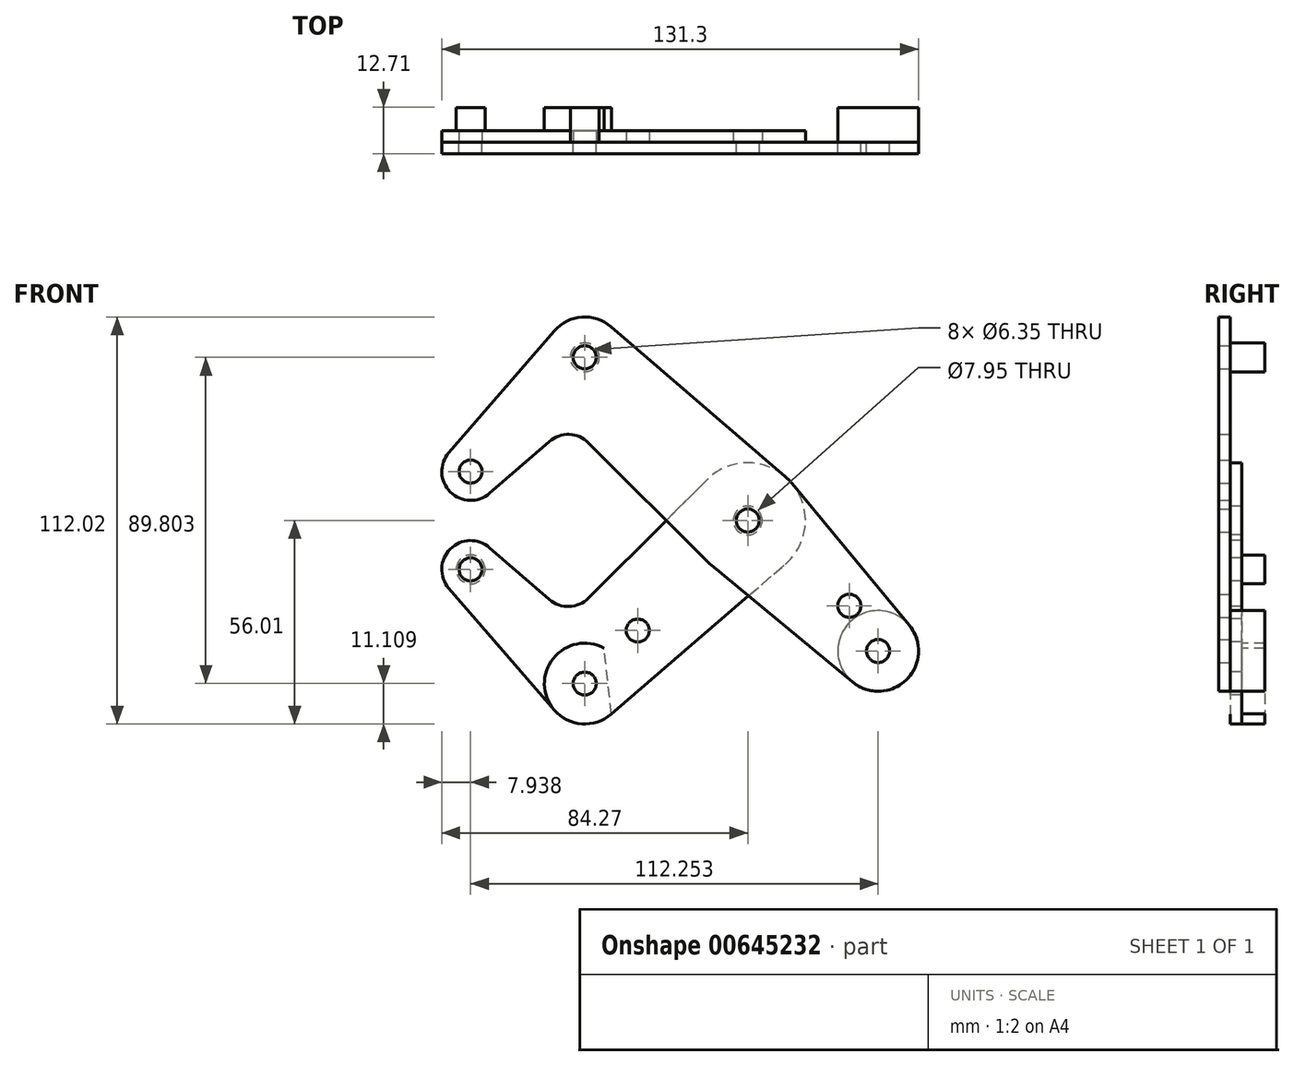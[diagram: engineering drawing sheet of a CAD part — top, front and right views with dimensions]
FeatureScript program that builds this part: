
annotation { "Feature Type Name" : "Feature", "Feature Type Description" : "" }
export const myFeature = defineFeature(function(context is Context, id is Id, definition is map)
    precondition{}
    {
        {
            var Q0;
            Q0=qCreatedBy(makeId("Front.planeOp"),FACE);
            var sketch = newSketch(context, id + "F0", { "sketchPlane" : qUnion([Q0])});
            skLineSegment(sketch, "E0", {"start": v(-76.33, 13.47) * mm, "end": v(-44.9, 44.9) * mm, "construction": true});
            skLineSegment(sketch, "E1", {"start": v(-44.9, 44.9) * mm, "end": v(35.92, -35.92) * mm, "construction": true});
            skCircle(sketch, "E2", {"center": v(-76.33, 13.47) * mm, "radius": 7.94 * mm});
            skCircle(sketch, "E3", {"center": v(-76.33, 13.47) * mm, "radius": 3.18 * mm});
            skCircle(sketch, "E4", {"center": v(-44.9, 44.9) * mm, "radius": 11.11 * mm});
            skCircle(sketch, "E5", {"center": v(-44.9, 44.9) * mm, "radius": 3.18 * mm});
            skCircle(sketch, "E6", {"center": v(0, 0) * mm, "radius": 15.88 * mm});
            skCircle(sketch, "E7", {"center": v(0, 0) * mm, "radius": 3.98 * mm});
            skCircle(sketch, "E8", {"center": v(0, 0) * mm, "radius": 3.18 * mm});
            skCircle(sketch, "E9", {"center": v(35.92, -35.92) * mm, "radius": 11.11 * mm});
            skCircle(sketch, "E10", {"center": v(35.92, -35.92) * mm, "radius": 3.18 * mm});
            skCircle(sketch, "E11", {"center": v(27.97, -23.48) * mm, "radius": 3.18 * mm});
            skLineSegment(sketch, "E12", {"start": v(0, 0) * mm, "end": v(-44.9, -44.9) * mm, "construction": true});
            skLineSegment(sketch, "E13", {"start": v(-44.9, -44.9) * mm, "end": v(-76.33, -13.47) * mm, "construction": true});
            skCircle(sketch, "E14", {"center": v(-76.33, -13.47) * mm, "radius": 7.94 * mm});
            skCircle(sketch, "E15", {"center": v(-76.33, -13.47) * mm, "radius": 3.18 * mm});
            skCircle(sketch, "E16", {"center": v(-44.9, -44.9) * mm, "radius": 11.11 * mm});
            skCircle(sketch, "E17", {"center": v(-44.9, -44.9) * mm, "radius": 3.18 * mm});
            skCircle(sketch, "E18", {"center": v(-30.3, -30.3) * mm, "radius": 3.18 * mm});
            skLineSegment(sketch, "E19", {"start": v(-76.33, 13.47) * mm, "end": v(-76.33, -13.47) * mm, "construction": true});
            skLineSegment(sketch, "E20", {"start": v(-82.33, 18.67) * mm, "end": v(-53.3, 52.18) * mm});
            skLineSegment(sketch, "E21", {"start": v(-71.13, 7.47) * mm, "end": v(-54.65, 21.76) * mm});
            skLineSegment(sketch, "E22", {"start": v(-37.66, 53.33) * mm, "end": v(10.35, 12.04) * mm});
            skLineSegment(sketch, "E23", {"start": v(44.48, -28.83) * mm, "end": v(12.23, 10.12) * mm});
            skLineSegment(sketch, "E24", {"start": v(-43.82, 21.37) * mm, "end": v(-11.23, -11.23) * mm});
            skLineSegment(sketch, "E25", {"start": v(28.83, -44.48) * mm, "end": v(-10.12, -12.23) * mm});
            skPoint(sketch, "E26.newPointA", {"position": v(-37.66, 36.48) * mm});
            skArc(sketch, "E26.filletArc", {"start": v(-43.82, 21.37) * mm, "mid": v(-49.16, 23.7) * mm, "end": v(-54.65, 21.76) * mm});
            skLineSegment(sketch, "E27", {"start": v(-82.33, -18.67) * mm, "end": v(-53.3, -52.18) * mm});
            skLineSegment(sketch, "E28", {"start": v(-37.66, -53.33) * mm, "end": v(11.26, -11.26) * mm});
            skLineSegment(sketch, "E29", {"start": v(-71.13, -7.47) * mm, "end": v(-54.65, -21.76) * mm});
            skLineSegment(sketch, "E30", {"start": v(-43.82, -21.37) * mm, "end": v(-11.23, 11.23) * mm});
            skArc(sketch, "E31.filletArc", {"start": v(-54.65, -21.76) * mm, "mid": v(-49.16, -23.7) * mm, "end": v(-43.82, -21.37) * mm});
            skSolve(sketch);
        }
        {
            var Q0;
            Q0=makeQuery(id+"F0.imprint","IMPRINT",FACE,{"disambiguationData":[TD([[makeQuery(id+"F0.imprint","IMPRINT",EDGE,{"derivedFrom":sQuery(id+"F0.wireOp",EDGE,"E3")}),-1.0]])]});
            var Q1;
            Q1=makeQuery(id+"F0.imprint","IMPRINT",FACE,{"disambiguationData":[TD([[makeQuery(id+"F0.imprint","IMPRINT",EDGE,{"derivedFrom":sQuery(id+"F0.wireOp",EDGE,"E5")}),-1.0]])]});
            var Q2;
            Q2=makeQuery(id+"F0.imprint","IMPRINT",FACE,{"disambiguationData":[TD([[makeQuery(id+"F0.imprint","IMPRINT",EDGE,{"derivedFrom":sQuery(id+"F0.wireOp",EDGE,"E10")}),-1.0]])]});
            var Q3;
            {var subQ0=sQuery(id+"F0.wireOp",EDGE,"E24");var subQ1=sQuery(id+"F0.wireOp",EDGE,"E6");var subQ2=makeQuery(id+"F0.imprint","INTERSECT",VERTEX,{"derivedFrom":[subQ1,subQ0]});Q3=makeQuery(id+"F0.imprint","IMPRINT",FACE,{"disambiguationData":[TD([[makeQuery(id+"F0.imprint","IMPRINT",EDGE,{"disambiguationData":[TD([[subQ2,1.0]])],"derivedFrom":subQ1}),-1.0]])]});}
            var Q4;
            {var subQ0=sQuery(id+"F0.wireOp",EDGE,"E25");var subQ1=sQuery(id+"F0.wireOp",EDGE,"E6");var subQ2=makeQuery(id+"F0.imprint","INTERSECT",VERTEX,{"derivedFrom":[subQ1,subQ0]});Q4=makeQuery(id+"F0.imprint","IMPRINT",FACE,{"disambiguationData":[TD([[makeQuery(id+"F0.imprint","IMPRINT",EDGE,{"disambiguationData":[TD([[subQ2,-1.0]])],"derivedFrom":subQ1}),-1.0]])]});}
            var Q5;
            Q5=makeQuery(id+"F0.imprint","IMPRINT",FACE,{"disambiguationData":[TD([[makeQuery(id+"F0.imprint","IMPRINT",EDGE,{"derivedFrom":sQuery(id+"F0.wireOp",EDGE,"E11")}),-1.0]])]});
            var Q6;
            Q6=makeQuery(id+"F0.imprint","IMPRINT",FACE,{"disambiguationData":[TD([[makeQuery(id+"F0.imprint","IMPRINT",EDGE,{"derivedFrom":sQuery(id+"F0.wireOp",EDGE,"E7")}),-1.0]])]});
            var Q7;
            Q7=makeQuery(id+"F0.imprint","IMPRINT",FACE,{"disambiguationData":[TD([[makeQuery(id+"F0.imprint","IMPRINT",EDGE,{"derivedFrom":sQuery(id+"F0.wireOp",EDGE,"E7")}),1.0]])]});
            var Q8;
            {var subQ0=sQuery(id+"F0.wireOp",EDGE,"E20");Q8=makeQuery(id+"F0.imprint","IMPRINT",FACE,{"disambiguationData":[TD([[makeQuery(id+"F0.imprint","IMPRINT",EDGE,{"derivedFrom":subQ0}),-1.0]])]});}
            extrude(context, id + "F1", {"entities" : qUnion([Q0, Q1, Q2, Q3, Q4, Q5, Q6, Q7, Q8]), "depth" : 3.17 * mm, "offsetDistance" : 25.4 * mm});
        }
        {
            var Q0;
            Q0=makeQuery(id+"F0.imprint","IMPRINT",FACE,{"disambiguationData":[TD([[makeQuery(id+"F0.imprint","IMPRINT",EDGE,{"derivedFrom":sQuery(id+"F0.wireOp",EDGE,"E18")}),-1.0]])]});
            var Q1;
            Q1=makeQuery(id+"F0.imprint","IMPRINT",FACE,{"disambiguationData":[TD([[makeQuery(id+"F0.imprint","IMPRINT",EDGE,{"derivedFrom":sQuery(id+"F0.wireOp",EDGE,"E15")}),-1.0]])]});
            var Q2;
            Q2=makeQuery(id+"F0.imprint","IMPRINT",FACE,{"disambiguationData":[TD([[makeQuery(id+"F0.imprint","IMPRINT",EDGE,{"derivedFrom":sQuery(id+"F0.wireOp",EDGE,"E17")}),-1.0]])]});
            var Q3;
            {var subQ0=sQuery(id+"F0.wireOp",EDGE,"E24");var subQ1=sQuery(id+"F0.wireOp",EDGE,"E6");var subQ2=makeQuery(id+"F0.imprint","INTERSECT",VERTEX,{"derivedFrom":[subQ1,subQ0]});Q3=makeQuery(id+"F0.imprint","IMPRINT",FACE,{"disambiguationData":[TD([[makeQuery(id+"F0.imprint","IMPRINT",EDGE,{"disambiguationData":[TD([[subQ2,1.0]])],"derivedFrom":subQ1}),-1.0]])]});}
            var Q4;
            Q4=makeQuery(id+"F0.imprint","IMPRINT",FACE,{"disambiguationData":[TD([[makeQuery(id+"F0.imprint","IMPRINT",EDGE,{"derivedFrom":sQuery(id+"F0.wireOp",EDGE,"E7")}),-1.0]])]});
            var Q5;
            {var subQ0=sQuery(id+"F0.wireOp",EDGE,"E25");var subQ1=sQuery(id+"F0.wireOp",EDGE,"E6");var subQ2=makeQuery(id+"F0.imprint","INTERSECT",VERTEX,{"derivedFrom":[subQ1,subQ0]});Q5=makeQuery(id+"F0.imprint","IMPRINT",FACE,{"disambiguationData":[TD([[makeQuery(id+"F0.imprint","IMPRINT",EDGE,{"disambiguationData":[TD([[subQ2,-1.0]])],"derivedFrom":subQ1}),-1.0]])]});}
            extrude(context, id + "F2", {"entities" : qUnion([Q0, Q1, Q2, Q3, Q4, Q5]), "oppositeDirection" : true, "depth" : 3.17 * mm, "offsetDistance" : 25.4 * mm});
        }
        {
            var Q0;
            Q0=makeQuery(id+"F1.opExtrude","CAP_FACE",FACE,{"disambiguationData":[OSD([sQuery(id+"F0.wireOp",EDGE,"E2"),sQuery(id+"F0.wireOp",EDGE,"E3"),sQuery(id+"F0.wireOp",EDGE,"E4"),sQuery(id+"F0.wireOp",EDGE,"E5"),sQuery(id+"F0.wireOp",EDGE,"E6"),sQuery(id+"F0.wireOp",EDGE,"E8"),sQuery(id+"F0.wireOp",EDGE,"E9"),sQuery(id+"F0.wireOp",EDGE,"E10"),sQuery(id+"F0.wireOp",EDGE,"E11"),sQuery(id+"F0.wireOp",EDGE,"E20"),sQuery(id+"F0.wireOp",EDGE,"E21"),sQuery(id+"F0.wireOp",EDGE,"E22"),sQuery(id+"F0.wireOp",EDGE,"E23"),sQuery(id+"F0.wireOp",EDGE,"E24"),sQuery(id+"F0.wireOp",EDGE,"E25"),sQuery(id+"F0.wireOp",EDGE,"E26.filletArc")])],"isStart":false});
            var sketch = newSketch(context, id + "F3", { "sketchPlane" : qUnion([Q0])});
            skCircle(sketch, "E32", {"center": v(-44.9, 44.9) * mm, "radius": 3.98 * mm});
            skCircle(sketch, "E33.0", {"center": v(35.92, -35.92) * mm, "radius": 11.11 * mm});
            skSolve(sketch);
        }
        {
            var Q0;
            Q0=makeQuery(id+"F0.imprint","IMPRINT",FACE,{"disambiguationData":[TD([[makeQuery(id+"F0.imprint","IMPRINT",EDGE,{"derivedFrom":sQuery(id+"F0.wireOp",EDGE,"E18")}),-1.0]])]});
            var sketch = newSketch(context, id + "F4", { "sketchPlane" : qUnion([Q0])});
            skCircle(sketch, "E34", {"center": v(-76.33, -13.47) * mm, "radius": 3.98 * mm});
            skArc(sketch, "E35.0", {"start": v(-39.6, -35.14) * mm, "mid": v(-55.95, -46.13) * mm, "end": v(-37.58, -53.26) * mm});
            skLineSegment(sketch, "E36", {"start": v(-44.9, -44.9) * mm, "end": v(35.92, -35.92) * mm, "construction": true});
            skLineSegment(sketch, "E37", {"start": v(-39.6, -35.14) * mm, "end": v(-37.58, -53.26) * mm});
            skSolve(sketch);
        }
        {
            var Q0;
            Q0=qCreatedBy(makeId("Front.planeOp"),FACE);
            cPlane(context, id + "F5", {"entities" : qUnion([Q0]), "cplaneType" : CPlaneType.OFFSET, "offset" : 9.52 * mm, "oppositeDirection" : true, "width" : 152.4 * mm, "height" : 152.4 * mm});
        }
        {
            var Q0;
            Q0 = qSketchRegion(id + "F3", true);
            var Q1;
            Q1 = qSketchRegion(id + "F4", true);
            var Q2;
            Q2=qCreatedBy(id+"F5.planeOp",FACE);
            extrude(context, id + "F6", {"entities" : qUnion([Q0, Q1]), "endBound" : BoundingType.UP_TO_SURFACE, "oppositeDirection" : true, "depth" : 25.4 * mm, "endBoundEntityFace" : qUnion([Q2]), "offsetDistance" : 25.4 * mm});
        }
        {
            var Q0;
            Q0=makeQuery(id+"F2.opExtrude","SWEPT_BODY",BODY,{"disambiguationData":[OSD([sQuery(id+"F0.wireOp",EDGE,"E6"),sQuery(id+"F0.wireOp",EDGE,"E7"),sQuery(id+"F0.wireOp",EDGE,"E14"),sQuery(id+"F0.wireOp",EDGE,"E15"),sQuery(id+"F0.wireOp",EDGE,"E16"),sQuery(id+"F0.wireOp",EDGE,"E17"),sQuery(id+"F0.wireOp",EDGE,"E18"),sQuery(id+"F0.wireOp",EDGE,"E27"),sQuery(id+"F0.wireOp",EDGE,"E28"),sQuery(id+"F0.wireOp",EDGE,"E29"),sQuery(id+"F0.wireOp",EDGE,"E30"),sQuery(id+"F0.wireOp",EDGE,"E31.filletArc")])]});
            var Q1;
            Q1=makeQuery(id+"F1.opExtrude","SWEPT_BODY",BODY,{"disambiguationData":[OSD([sQuery(id+"F0.wireOp",EDGE,"E2"),sQuery(id+"F0.wireOp",EDGE,"E3"),sQuery(id+"F0.wireOp",EDGE,"E4"),sQuery(id+"F0.wireOp",EDGE,"E5"),sQuery(id+"F0.wireOp",EDGE,"E6"),sQuery(id+"F0.wireOp",EDGE,"E8"),sQuery(id+"F0.wireOp",EDGE,"E9"),sQuery(id+"F0.wireOp",EDGE,"E10"),sQuery(id+"F0.wireOp",EDGE,"E11"),sQuery(id+"F0.wireOp",EDGE,"E20"),sQuery(id+"F0.wireOp",EDGE,"E21"),sQuery(id+"F0.wireOp",EDGE,"E22"),sQuery(id+"F0.wireOp",EDGE,"E23"),sQuery(id+"F0.wireOp",EDGE,"E24"),sQuery(id+"F0.wireOp",EDGE,"E25"),sQuery(id+"F0.wireOp",EDGE,"E26.filletArc")])]});
            var Q2;
            Q2=makeQuery(id+"F6.opExtrude","SWEPT_BODY",BODY,{"disambiguationData":[OSD([sQuery(id+"F3.wireOp",EDGE,"E32")])]});
            var Q3;
            Q3=makeQuery(id+"F6.opExtrude","SWEPT_BODY",BODY,{"disambiguationData":[OSD([sQuery(id+"F4.wireOp",EDGE,"E34")])]});
            var Q4;
            Q4=makeQuery(id+"F6.opExtrude","SWEPT_BODY",BODY,{"disambiguationData":[OSD([sQuery(id+"F4.wireOp",EDGE,"E35.0"),sQuery(id+"F4.wireOp",EDGE,"E37")])]});
            var Q5;
            Q5=makeQuery(id+"F6.opExtrude","SWEPT_BODY",BODY,{"disambiguationData":[OSD([sQuery(id+"F3.wireOp",EDGE,"E33.0")])]});
            booleanBodies(context, id + "F7", {"operationType" : BooleanOperationType.SUBTRACTION, "tools" : qUnion([Q0, Q1]), "targets" : qUnion([Q2, Q3, Q4, Q5]), "keepTools" : true});
        }
    });
